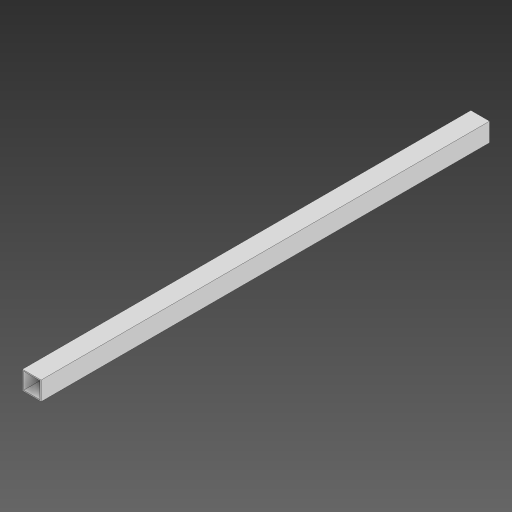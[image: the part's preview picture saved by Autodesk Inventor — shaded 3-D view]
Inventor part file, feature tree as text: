
AUTODESK INVENTOR PART (.ipt)
format: ipt  version: 2024 (Build 280153000, 153)  size: 91,648 bytes
history: native  units: in
note: dims shown in document units (in); Inventor stores cm internally (conversion verified against a paired STEP export)
features: extrude x1, sketch x1
ambient origin geometry x8: Origin, YZ Plane, XZ Plane, XY Plane, X Axis, Y Axis, Z Axis, Center Point
bodies: Solid1 (feature_tree)
feature tree (2):
  extrude  "Extrusion1"  Depth=1.0in
  sketch  "Sketch1"  dims[d0=1.0in d1=1.0in d2=0.0625in d3=24.0in d4=0.0in]
